# Revit family: Дверь.Alumark_однопольная с глухим окном_S44
name_source: partatom
category: Двери
revit_build: Autodesk Revit 2017 (Build: 20171027_0315(x64)
units: mm (PartAtom-declared; Revit-internal decimal feet)

## family parameters
Всегда вертикально = Да
Заголовок OmniClass = Doors
Номер OmniClass = 23.30.10.00
Общий = Нет
Основа = Стена
При загрузке вырезать с полостями = Нет
Точка расчета площади = Нет

## types (4) — shared parameters
ADSK_Завод-изготовитель = ТБМ
ADSK_Обозначение = ГОСТ 23747-2015
URL = http://www.tbm.ru
sp_energy = Энергосберегающие стекла
sp_gaz = Заполненный газом
sp_standart = Обычный стеклопакет
Аналитическая конструкция = Застеклённая створчатая дверь, металлическая рама с двумя стеклами
Высота импоста = 800 мм
Дверь с цоколем = Нет
Заполнение стеклопакета = Обычный стеклопакет
Изготовитель = ТБМ
Изображение типоразмера = схема_дверь_фрамуга.png
Импост двери = Нет
Коэффициент теплопередачи (U) = 4.2812 Вт/(м²·K)
Материал остекления = <По категории>
Материал профилей = <По категории>
Материал фурнитуры = <По категории>
Окно высота = 300 мм
Описание = Дверь Проем ТБМ
Примерная высота = 2380 мм
Примерная ширина = 860 мм
Разработчик = ООО ПРОРУБИМ
Разработчик (телефон) = +7(495)649-85-43
ТБМ_Артикул_Импост = ALM244301
ТБМ_Артикул_Крепление порога = ALM744630
ТБМ_Артикул_Подкладка под СП = ALM744307
ТБМ_Артикул_Порог = ALM244391
ТБМ_Артикул_Притвор = ALM244806
ТБМ_Артикул_Рама = ALM244100
ТБМ_Артикул_Распорный штифт = ALM885014
ТБМ_Артикул_Съемный ус = ALM244803
ТБМ_Артикул_Т-соединитель рамы = ALM744601
ТБМ_Артикул_Угловой соединитель рамы = ALM770421
ТБМ_Артикул_Уголок выравнивающий = ALM744014
ТБМ_Артикул_Уголок выравнивающий 2 = ALM744008
ТБМ_Артикул_Уплотнитель внутренний = ALM770207
ТБМ_Артикул_Уплотнитель наружный = ALM770004
ТБМ_Артикул_Уплотнитель порога = ELM0336
ТБМ_Артикул_Уплотнитель притвора = ALM770020
ТБМ_Артикул_Штапик = ALM244006
ТБМ_Длина_Импост = 768 мм
ТБМ_Длина_Порог = 760 мм
ТБМ_Длина_Притвор = 4928 мм
ТБМ_Длина_Рама = 5620 мм
ТБМ_Длина_Створка = 5574 мм
ТБМ_Длина_Съемный ус = 1208 мм
ТБМ_Длина_Уплотнитель внутренний = 6174 мм
ТБМ_Длина_Уплотнитель наружный = 6174 мм
ТБМ_Длина_Уплотнитель порога = 760 мм
ТБМ_Длина_Уплотнитель притвора = 11454 мм
ТБМ_Длина_Штапик = 7010 мм
ТБМ_Количество_Крепление порога = 1
ТБМ_Количество_Подкладка под СП = 8
ТБМ_Количество_Распорный штифт = 12
ТБМ_Количество_Т-соединитель рамы = 1
ТБМ_Количество_Угловой соединитель рамы = 6
ТБМ_Количество_Уголок выравнивающий = 4
ТБМ_Количество_Уголок выравнивающий 2 = 4
ТБМ_Площадь стеклопакета = 1.36 м²
ТБМ_Стеклопакет_Высота 1 = 2172 мм
ТБМ_Стеклопакет_Ширина 1 = 624 мм
Термостойкость = 0.2336 (м²·K)/Вт
Тип стеклопакета = 24мм 1-камерный
Толщина = 44 мм
Функция = Наружные слои
высота фурнитуры = 2111 мм
импост_ширина = 62 мм
рама_ширина = 66 мм
сп_16_мм = 16мм 1-камерный
сп_24_мм = 24мм 1-камерный
створка_ширина = 84 мм
таблица выбора = каталог ТБМ однопольная дверь S44
штапик_толщина = 12 мм
zero-valued in all types: Коэффициент теплопритока от солнечного излучения, Пропускание видимого света, ТБМ_Длина_Притвор цоколя, ТБМ_Длина_Цоколь, ТБМ_Количество_Т-соединитель цоколя

## per-type parameters (varying)
| type | ADSK_Наименование | Левая | Открывание внутрь | Открывание наружу | Правая | ТБМ_Артикул_Створка | левая_внутрь | левая_наружу | номер профиля | правая_внутрь | правая_наружу |
| 860х2380 Правая Открывание наружу (СП 24мм Обычный) | ДАН О Оп Пр Р (Однокамерный стеклопакет 24 мм) | Нет | Нет | Да | Да | ALM244281 | Нет | Нет | 11101 | Нет | Да |
| 860х2380 Левая Открывание наружу (СП 24мм Обычный) | ДАН О Оп Л Р (Однокамерный стеклопакет 24 мм) | Да | Нет | Да | Нет | ALM244281 | Нет | Да | 12101 | Нет | Нет |
| 860х2380 Правая Открывание внутрь (СП 24мм Обычный) | ДАВ О Оп Пр Р (Однокамерный стеклопакет 24 мм) | Нет | Да | Нет | Да | ALM244280 | Нет | Нет | 21101 | Да | Нет |
| 860х2380 Левая Открывание внутрь (СП 24мм Обычный) | ДАВ О Оп Л Р (Однокамерный стеклопакет 24 мм) | Да | Да | Нет | Нет | ALM244280 | Да | Нет | 22101 | Нет | Нет |
